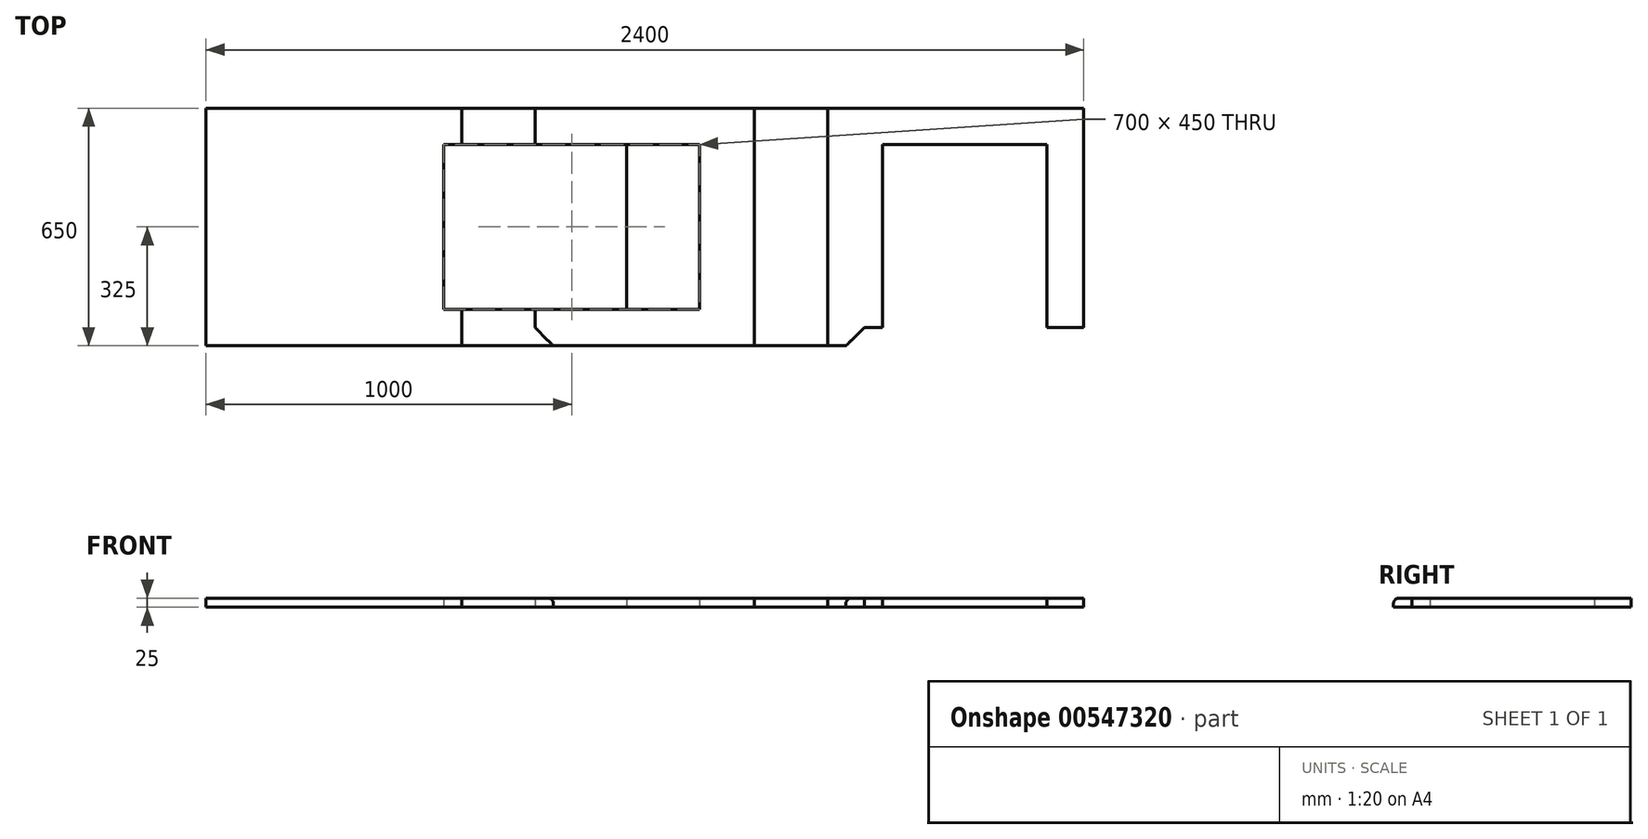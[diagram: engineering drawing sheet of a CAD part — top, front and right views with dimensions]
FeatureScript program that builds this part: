
annotation { "Feature Type Name" : "Feature", "Feature Type Description" : "" }
export const myFeature = defineFeature(function(context is Context, id is Id, definition is map)
    precondition{}
    {
        {
            var Q0;
            Q0=qCreatedBy(makeId("Top.planeOp"),FACE);
            var sketch = newSketch(context, id + "F0", { "sketchPlane" : qUnion([Q0])});
            skLineSegment(sketch, "E0.bottom", {"start": v(1200, -325) * mm, "end": v(-1200, -325) * mm});
            skLineSegment(sketch, "E0.top", {"start": v(1200, 325) * mm, "end": v(-1200, 325) * mm});
            skLineSegment(sketch, "E0.left", {"start": v(1200, -325) * mm, "end": v(1200, 325) * mm});
            skLineSegment(sketch, "E0.right", {"start": v(-1200, -325) * mm, "end": v(-1200, 325) * mm});
            skPoint(sketch, "E0.middle", {"position": v(0, 0) * mm});
            skSolve(sketch);
        }
        {
            var Q0;
            Q0=makeQuery(id+"F0.imprint","IMPRINT",FACE,{"disambiguationData":[TD([[makeQuery(id+"F0.imprint","IMPRINT",EDGE,{"derivedFrom":sQuery(id+"F0.wireOp",EDGE,"E0.bottom")}),-1.0]])]});
            extrude(context, id + "F1", {"entities" : qUnion([Q0]), "endBound" : BoundingType.SYMMETRIC, "depth" : 25 * mm, "offsetDistance" : 25 * mm});
        }
        {
            var Q0;
            Q0=makeQuery(id+"F1.opExtrude","CAP_EDGE",EDGE,{"disambiguationData":[OSD([sQuery(id+"F0.wireOp",EDGE,"E0.bottom")])],"isStart":false});
            fillet(context, id + "F2", {"entities" : qUnion([Q0]), "radius" : 15 * mm, "tangentPropagation" : true, "allowEdgeOverflow" : false});
        }
        {
            var Q0;
            Q0=makeQuery(id+"F1.opExtrude","CAP_FACE",FACE,{"disambiguationData":[OSD([sQuery(id+"F0.wireOp",EDGE,"E0.bottom"),sQuery(id+"F0.wireOp",EDGE,"E0.top"),sQuery(id+"F0.wireOp",EDGE,"E0.left"),sQuery(id+"F0.wireOp",EDGE,"E0.right")])],"isStart":true});
            var sketch = newSketch(context, id + "F3", { "sketchPlane" : qUnion([Q0])});
            skLineSegment(sketch, "E1.0", {"start": v(1200, 325) * mm, "end": v(-1200, 325) * mm});
            skLineSegment(sketch, "E2.0", {"start": v(1200, 325) * mm, "end": v(1200, -325) * mm});
            skLineSegment(sketch, "E3", {"start": v(1200, 275) * mm, "end": v(600, 275) * mm});
            skLineSegment(sketch, "E4", {"start": v(600, 275) * mm, "end": v(550, 325) * mm});
            skSolve(sketch);
        }
        {
            var Q0;
            {var subQ4=sQuery(id+"F3.wireOp",EDGE,"E3");Q0=makeQuery(id+"F3.imprint","IMPRINT",FACE,{"disambiguationData":[TD([[makeQuery(id+"F3.imprint","IMPRINT",EDGE,{"derivedFrom":subQ4}),-1.0]])]});}
            extrude(context, id + "F4", {"entities" : qUnion([Q0]), "operationType" : NewBodyOperationType.REMOVE, "endBound" : BoundingType.THROUGH_ALL, "oppositeDirection" : true, "depth" : 25 * mm, "offsetDistance" : 25 * mm});
        }
        {
            var Q0;
            Q0=qCreatedBy(makeId("Top.planeOp"),FACE);
            var sketch = newSketch(context, id + "F5", { "sketchPlane" : qUnion([Q0])});
            skLineSegment(sketch, "E5.bottom", {"start": v(300, -325) * mm, "end": v(-300, -325) * mm});
            skLineSegment(sketch, "E5.top", {"start": v(300, 325) * mm, "end": v(-300, 325) * mm});
            skLineSegment(sketch, "E5.left", {"start": v(300, -325) * mm, "end": v(300, 325) * mm});
            skLineSegment(sketch, "E5.right", {"start": v(-300, -325) * mm, "end": v(-300, 325) * mm});
            skPoint(sketch, "E5.middle", {"position": v(0, 0) * mm});
            skLineSegment(sketch, "E6", {"start": v(-250, -325) * mm, "end": v(-300, -275) * mm});
            skSolve(sketch);
        }
        {
            var Q0;
            {var subQ1=sQuery(id+"F5.wireOp",EDGE,"E5.top");Q0=makeQuery(id+"F5.imprint","IMPRINT",FACE,{"disambiguationData":[TD([[makeQuery(id+"F5.imprint","IMPRINT",EDGE,{"derivedFrom":subQ1}),1.0]])]});}
            extrude(context, id + "F6", {"entities" : qUnion([Q0]), "endBound" : BoundingType.SYMMETRIC, "depth" : 25 * mm, "offsetDistance" : 25 * mm});
        }
        {
            var Q0;
            Q0=makeQuery(id+"F6.opExtrude","CAP_EDGE",EDGE,{"disambiguationData":[OSD([sQuery(id+"F5.wireOp",EDGE,"E5.bottom")])],"isStart":false});
            fillet(context, id + "F7", {"entities" : qUnion([Q0]), "radius" : 15 * mm, "tangentPropagation" : true, "allowEdgeOverflow" : false});
        }
        {
            var Q0;
            Q0=makeQuery(id+"F1.opExtrude","CAP_FACE",FACE,{"disambiguationData":[OSD([sQuery(id+"F0.wireOp",EDGE,"E0.bottom"),sQuery(id+"F0.wireOp",EDGE,"E0.top"),sQuery(id+"F0.wireOp",EDGE,"E0.left"),sQuery(id+"F0.wireOp",EDGE,"E0.right")])],"isStart":true});
            var sketch = newSketch(context, id + "F8", { "sketchPlane" : qUnion([Q0])});
            skLineSegment(sketch, "E7.bottom", {"start": v(1100, -225) * mm, "end": v(650, -225) * mm});
            skLineSegment(sketch, "E7.top", {"start": v(1100, 575) * mm, "end": v(650, 575) * mm});
            skLineSegment(sketch, "E7.left", {"start": v(1100, -225) * mm, "end": v(1100, 575) * mm});
            skLineSegment(sketch, "E7.right", {"start": v(650, -225) * mm, "end": v(650, 575) * mm});
            skSolve(sketch);
        }
        {
            var Q0;
            {var subQ0=sQuery(id+"F8.wireOp",EDGE,"E7.bottom");Q0=makeQuery(id+"F8.imprint","IMPRINT",FACE,{"disambiguationData":[TD([[makeQuery(id+"F8.imprint","IMPRINT",EDGE,{"derivedFrom":subQ0}),-1.0]])]});}
            extrude(context, id + "F9", {"entities" : qUnion([Q0]), "operationType" : NewBodyOperationType.REMOVE, "endBound" : BoundingType.THROUGH_ALL, "oppositeDirection" : true, "depth" : 25 * mm, "offsetDistance" : 25 * mm});
        }
        {
            var Q0;
            Q0=makeQuery(id+"F6.opExtrude","CAP_FACE",FACE,{"disambiguationData":[OSD([sQuery(id+"F5.wireOp",EDGE,"E5.bottom"),sQuery(id+"F5.wireOp",EDGE,"E5.top"),sQuery(id+"F5.wireOp",EDGE,"E5.left"),sQuery(id+"F5.wireOp",EDGE,"E5.right"),sQuery(id+"F5.wireOp",EDGE,"E6")])],"isStart":true});
            var sketch = newSketch(context, id + "F10", { "sketchPlane" : qUnion([Q0])});
            skLineSegment(sketch, "E8.bottom", {"start": v(-300, -225) * mm, "end": v(150, -225) * mm});
            skLineSegment(sketch, "E8.top", {"start": v(-300, 225) * mm, "end": v(150, 225) * mm});
            skLineSegment(sketch, "E8.left", {"start": v(-300, -225) * mm, "end": v(-300, 225) * mm});
            skLineSegment(sketch, "E8.right", {"start": v(150, -225) * mm, "end": v(150, 225) * mm});
            skSolve(sketch);
        }
        {
            var Q0;
            Q0=makeQuery(id+"F10.imprint","IMPRINT",FACE,{"disambiguationData":[TD([[makeQuery(id+"F10.imprint","IMPRINT",EDGE,{"derivedFrom":sQuery(id+"F10.wireOp",EDGE,"E8.bottom")}),1.0]])]});
            extrude(context, id + "F11", {"entities" : qUnion([Q0]), "operationType" : NewBodyOperationType.REMOVE, "endBound" : BoundingType.THROUGH_ALL, "oppositeDirection" : true, "depth" : 25 * mm, "offsetDistance" : 25 * mm});
        }
        {
            var Q0;
            Q0=qCreatedBy(makeId("Top.planeOp"),FACE);
            var sketch = newSketch(context, id + "F12", { "sketchPlane" : qUnion([Q0])});
            skLineSegment(sketch, "E9.bottom", {"start": v(500, -325) * mm, "end": v(-500, -325) * mm});
            skLineSegment(sketch, "E9.top", {"start": v(500, 325) * mm, "end": v(-500, 325) * mm});
            skLineSegment(sketch, "E9.left", {"start": v(500, -325) * mm, "end": v(500, 325) * mm});
            skLineSegment(sketch, "E9.right", {"start": v(-500, -325) * mm, "end": v(-500, 325) * mm});
            skPoint(sketch, "E9.middle", {"position": v(0, 0) * mm});
            skSolve(sketch);
        }
        {
            var Q0;
            Q0=makeQuery(id+"F12.imprint","IMPRINT",FACE,{"disambiguationData":[TD([[makeQuery(id+"F12.imprint","IMPRINT",EDGE,{"derivedFrom":sQuery(id+"F12.wireOp",EDGE,"E9.bottom")}),-1.0]])]});
            extrude(context, id + "F13", {"entities" : qUnion([Q0]), "endBound" : BoundingType.SYMMETRIC, "depth" : 25 * mm, "offsetDistance" : 25 * mm});
        }
        {
            var Q0;
            Q0=makeQuery(id+"F13.opExtrude","CAP_EDGE",EDGE,{"disambiguationData":[OSD([sQuery(id+"F12.wireOp",EDGE,"E9.bottom")])],"isStart":false});
            fillet(context, id + "F14", {"entities" : qUnion([Q0]), "radius" : 15 * mm, "tangentPropagation" : true, "allowEdgeOverflow" : false});
        }
        {
            var Q0;
            Q0=makeQuery(id+"F1.opExtrude","CAP_FACE",FACE,{"disambiguationData":[OSD([sQuery(id+"F0.wireOp",EDGE,"E0.bottom"),sQuery(id+"F0.wireOp",EDGE,"E0.top"),sQuery(id+"F0.wireOp",EDGE,"E0.left"),sQuery(id+"F0.wireOp",EDGE,"E0.right")])],"isStart":true});
            var sketch = newSketch(context, id + "F15", { "sketchPlane" : qUnion([Q0])});
            skLineSegment(sketch, "E10.bottom", {"start": v(-550, 225) * mm, "end": v(-50, 225) * mm});
            skLineSegment(sketch, "E10.top", {"start": v(-550, -225) * mm, "end": v(-50, -225) * mm});
            skLineSegment(sketch, "E10.left", {"start": v(-550, 225) * mm, "end": v(-550, -225) * mm});
            skLineSegment(sketch, "E10.right", {"start": v(-50, 225) * mm, "end": v(-50, -225) * mm});
            skSolve(sketch);
        }
        {
            var Q0;
            Q0=makeQuery(id+"F15.imprint","IMPRINT",FACE,{"disambiguationData":[TD([[makeQuery(id+"F15.imprint","IMPRINT",EDGE,{"derivedFrom":sQuery(id+"F15.wireOp",EDGE,"E10.bottom")}),-1.0]])]});
            extrude(context, id + "F16", {"entities" : qUnion([Q0]), "operationType" : NewBodyOperationType.REMOVE, "endBound" : BoundingType.THROUGH_ALL, "oppositeDirection" : true, "depth" : 25 * mm, "offsetDistance" : 25 * mm});
        }
    });
